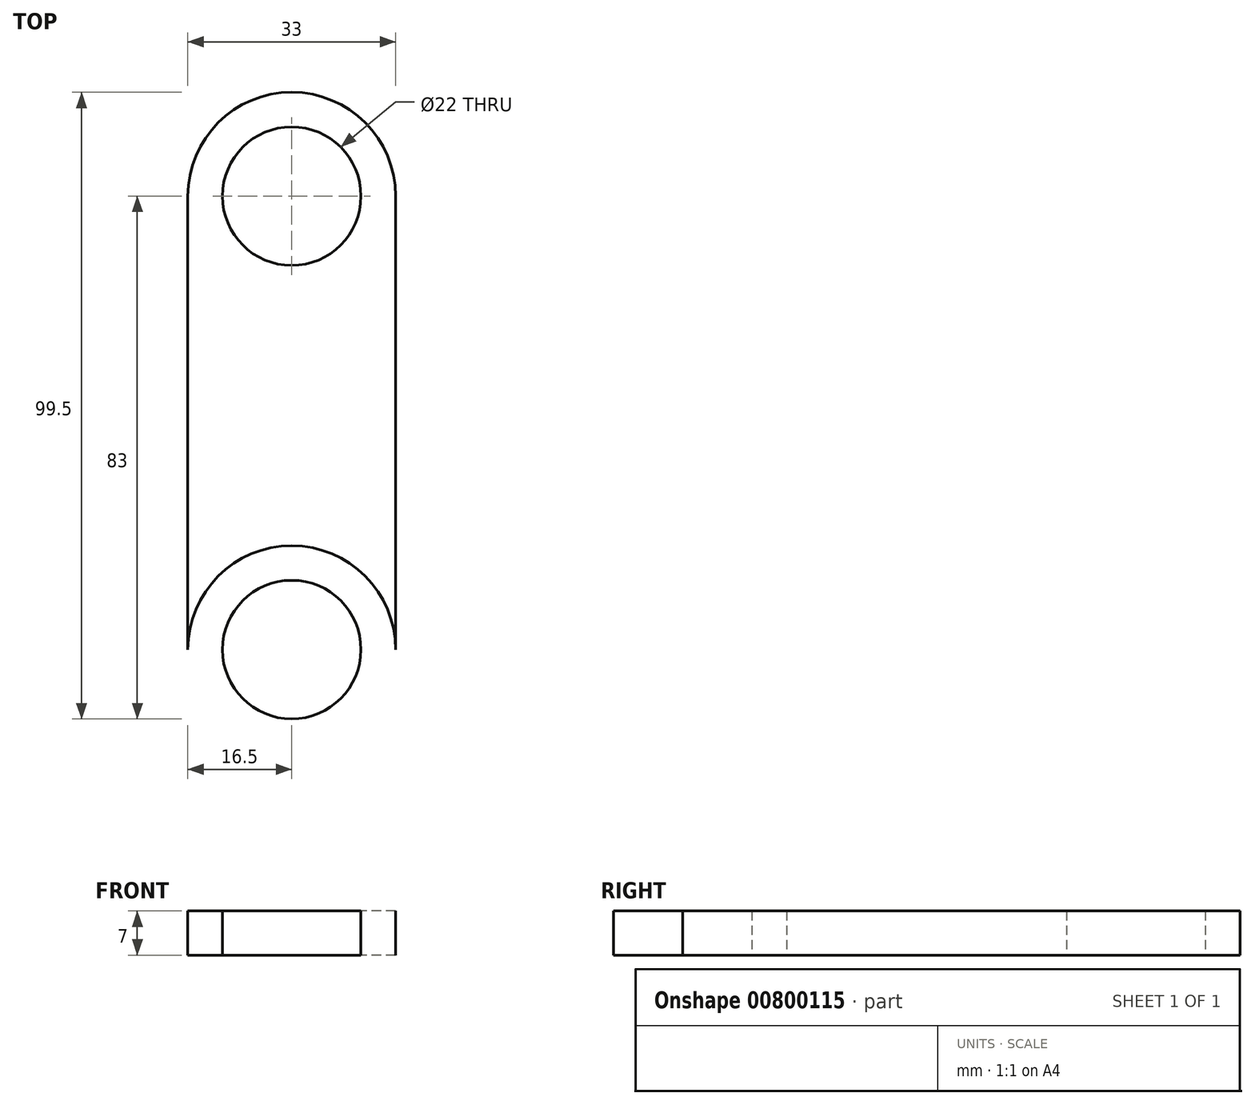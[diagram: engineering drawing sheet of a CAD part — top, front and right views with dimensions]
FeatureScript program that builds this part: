
annotation { "Feature Type Name" : "Feature", "Feature Type Description" : "" }
export const myFeature = defineFeature(function(context is Context, id is Id, definition is map)
    precondition{}
    {
        {
            var Q0;
            Q0=qCreatedBy(makeId("Top.planeOp"),FACE);
            var sketch = newSketch(context, id + "F0", { "sketchPlane" : qUnion([Q0])});
            skCircle(sketch, "E0", {"center": v(0, 0) * mm, "radius": 11 * mm});
            skCircle(sketch, "E1", {"center": v(0, 0) * mm, "radius": 16.5 * mm});
            skLineSegment(sketch, "E2", {"start": v(0, 0) * mm, "end": v(0, 36) * mm});
            skCircle(sketch, "E3", {"center": v(0, 36) * mm, "radius": 11 * mm});
            skCircle(sketch, "E4", {"center": v(0, 36) * mm, "radius": 16.5 * mm});
            skLineSegment(sketch, "E5", {"start": v(-16.5, 36) * mm, "end": v(-16.5, 0) * mm});
            skLineSegment(sketch, "E6", {"start": v(16.5, 36) * mm, "end": v(16.5, 0) * mm});
            skCircle(sketch, "E7.MirrorC", {"center": v(0, -36) * mm, "radius": 16.5 * mm});
            skCircle(sketch, "E8.MirrorC", {"center": v(0, -36) * mm, "radius": 11 * mm});
            skLineSegment(sketch, "E9.MirrorCS", {"start": v(-16.5, -36) * mm, "end": v(-16.5, 0) * mm});
            skLineSegment(sketch, "E10.MirrorCS", {"start": v(16.5, -36) * mm, "end": v(16.5, 0) * mm});
            skLineSegment(sketch, "E11.MirrorCS", {"start": v(0, 0) * mm, "end": v(0, -36) * mm});
            skSolve(sketch);
        }
        {
            var Q0;
            Q0=makeQuery(id+"F0.imprint","IMPRINT",FACE,{"disambiguationData":[TD([[makeQuery(id+"F0.imprint","IMPRINT",EDGE,{"derivedFrom":sQuery(id+"F0.wireOp",EDGE,"E3")}),-1.0]])]});
            var Q1;
            {var subQ0=sQuery(id+"F0.wireOp",EDGE,"E5");Q1=makeQuery(id+"F0.imprint","IMPRINT",FACE,{"disambiguationData":[TD([[makeQuery(id+"F0.imprint","IMPRINT",EDGE,{"derivedFrom":subQ0}),1.0]])]});}
            var Q2;
            Q2=makeQuery(id+"F0.imprint","IMPRINT",FACE,{"disambiguationData":[TD([[makeQuery(id+"F0.imprint","IMPRINT",EDGE,{"derivedFrom":sQuery(id+"F0.wireOp",EDGE,"E0")}),-1.0]])]});
            var Q3;
            {var subQ0=sQuery(id+"F0.wireOp",EDGE,"E6");Q3=makeQuery(id+"F0.imprint","IMPRINT",FACE,{"disambiguationData":[TD([[makeQuery(id+"F0.imprint","IMPRINT",EDGE,{"derivedFrom":subQ0}),-1.0]])]});}
            var Q4;
            Q4=makeQuery(id+"F0.imprint","IMPRINT",FACE,{"disambiguationData":[TD([[makeQuery(id+"F0.imprint","IMPRINT",EDGE,{"derivedFrom":sQuery(id+"F0.wireOp",EDGE,"w59R6iEj-CVUa-9ueu-Tdas-qJSk46i4Kriu")}),-1.0]])]});
            var Q5;
            {var subQ0=sQuery(id+"F0.wireOp",EDGE,"9POMkXtT-UIhR-gZSc-IBxU-MhUZsLWMQHKa");Q5=makeQuery(id+"F0.imprint","IMPRINT",FACE,{"disambiguationData":[TD([[makeQuery(id+"F0.imprint","IMPRINT",EDGE,{"derivedFrom":subQ0}),1.0]])]});}
            var Q6;
            {var subQ0=sQuery(id+"F0.wireOp",EDGE,"YCNqZ2w3-WSpD-Hsbr-H4GR-OdnoBN2QN9m9");Q6=makeQuery(id+"F0.imprint","IMPRINT",FACE,{"disambiguationData":[TD([[makeQuery(id+"F0.imprint","IMPRINT",EDGE,{"derivedFrom":subQ0}),-1.0]])]});}
            var Q7;
            {var subQ0=sQuery(id+"F0.wireOp",EDGE,"OA4v10v7-7EfV-4VX5-mn84-gwHHFcdyXIMs");Q7=makeQuery(id+"F0.imprint","IMPRINT",FACE,{"disambiguationData":[TD([[makeQuery(id+"F0.imprint","IMPRINT",EDGE,{"derivedFrom":subQ0}),1.0]])]});}
            var Q8;
            {var subQ0=sQuery(id+"F0.wireOp",EDGE,"jbeIYnq7-oU1V-4uXr-7pWT-a0tOQSGMHwd7");Q8=makeQuery(id+"F0.imprint","IMPRINT",FACE,{"disambiguationData":[TD([[makeQuery(id+"F0.imprint","IMPRINT",EDGE,{"derivedFrom":subQ0}),-1.0]])]});}
            var Q9;
            Q9=makeQuery(id+"F0.imprint","IMPRINT",FACE,{"disambiguationData":[TD([[makeQuery(id+"F0.imprint","IMPRINT",EDGE,{"derivedFrom":sQuery(id+"F0.wireOp",EDGE,"yAsJW6Uh-ad33-APdP-WKjL-GoX4Km3I4IXD")}),-1.0]])]});
            var Q10;
            {var subQ1=sQuery(id+"F0.wireOp",EDGE,"E0");var subQ6=sQuery(id+"F0.wireOp",EDGE,"4abtu9ri-UXn3-SYOI-gj1q-We8Vol63bBBD");var subQ8=makeQuery(id+"F0.imprint","INTERSECT",VERTEX,{"derivedFrom":[subQ1,subQ6]});Q10=makeQuery(id+"F0.imprint","IMPRINT",FACE,{"disambiguationData":[TD([[makeQuery(id+"F0.imprint","IMPRINT",EDGE,{"disambiguationData":[TD([[subQ8,1.0]])],"derivedFrom":subQ1}),-1.0]])]});}
            var Q11;
            {var subQ0=sQuery(id+"F0.wireOp",EDGE,"E2");var subQ1=sQuery(id+"F0.wireOp",EDGE,"E0");var subQ2=makeQuery(id+"F0.imprint","INTERSECT",VERTEX,{"derivedFrom":[subQ1,subQ0]});Q11=makeQuery(id+"F0.imprint","IMPRINT",FACE,{"disambiguationData":[TD([[makeQuery(id+"F0.imprint","IMPRINT",EDGE,{"disambiguationData":[TD([[subQ2,1.0]])],"derivedFrom":subQ1}),-1.0]])]});}
            var Q12;
            {var subQ0=sQuery(id+"F0.wireOp",EDGE,"4abtu9ri-UXn3-SYOI-gj1q-We8Vol63bBBD");var subQ1=sQuery(id+"F0.wireOp",EDGE,"E1");var subQ2=makeQuery(id+"F0.imprint","INTERSECT",VERTEX,{"derivedFrom":[subQ1,subQ0]});Q12=makeQuery(id+"F0.imprint","IMPRINT",FACE,{"disambiguationData":[TD([[makeQuery(id+"F0.imprint","IMPRINT",EDGE,{"disambiguationData":[TD([[subQ2,-1.0]])],"derivedFrom":subQ1}),-1.0]])]});}
            var Q13;
            Q13=makeQuery(id+"F0.imprint","IMPRINT",FACE,{"disambiguationData":[TD([[makeQuery(id+"F0.imprint","IMPRINT",EDGE,{"derivedFrom":sQuery(id+"F0.wireOp",EDGE,"gPTZF1Z9-XTqS-HgNZ-dHx2-uuJqNWMW2OWi")}),-1.0]])]});
            var Q14;
            Q14=makeQuery(id+"F0.imprint","IMPRINT",FACE,{"disambiguationData":[TD([[makeQuery(id+"F0.imprint","IMPRINT",EDGE,{"derivedFrom":sQuery(id+"F0.wireOp",EDGE,"pRESw98m-a7WB-Kv5g-NeYZ-crrq8cEqRvqA")}),-1.0]])]});
            var Q15;
            {var subQ0=sQuery(id+"F0.wireOp",EDGE,"UsmJrRAo-XE7W-iZRG-moOh-7sXpja8KDNIC");Q15=makeQuery(id+"F0.imprint","IMPRINT",FACE,{"disambiguationData":[TD([[makeQuery(id+"F0.imprint","IMPRINT",EDGE,{"derivedFrom":subQ0}),1.0]])]});}
            var Q16;
            {var subQ0=sQuery(id+"F0.wireOp",EDGE,"VRhz7LU3-4j0L-Ptb6-b6TJ-dEu7l9a6t27P");Q16=makeQuery(id+"F0.imprint","IMPRINT",FACE,{"disambiguationData":[TD([[makeQuery(id+"F0.imprint","IMPRINT",EDGE,{"derivedFrom":subQ0}),-1.0]])]});}
            var Q17;
            {var subQ5=sQuery(id+"F0.wireOp",EDGE,"E0");var subQ7=sQuery(id+"F0.wireOp",EDGE,"kRj30VAH-6UNE-fOCm-j82z-aHaWqIesx49l");var subQ9=makeQuery(id+"F0.imprint","INTERSECT",VERTEX,{"derivedFrom":[subQ5,subQ7]});Q17=makeQuery(id+"F0.imprint","IMPRINT",FACE,{"disambiguationData":[TD([[makeQuery(id+"F0.imprint","IMPRINT",EDGE,{"disambiguationData":[TD([[subQ9,-1.0]])],"derivedFrom":subQ5}),-1.0]])]});}
            var Q18;
            Q18=makeQuery(id+"F0.imprint","IMPRINT",FACE,{"disambiguationData":[TD([[makeQuery(id+"F0.imprint","IMPRINT",EDGE,{"derivedFrom":sQuery(id+"F0.wireOp",EDGE,"upXqz5X1-IKzU-vpSb-smbU-0F3NzNdugzUz")}),-1.0]])]});
            var Q19;
            {var subQ3=sQuery(id+"F0.wireOp",EDGE,"llwqtmrq-Y6AM-Iq4E-WuEU-azelPJxb1tUK");var subQ7=sQuery(id+"F0.wireOp",EDGE,"E1");var subQ9=makeQuery(id+"F0.imprint","INTERSECT",VERTEX,{"derivedFrom":[subQ7,subQ3]});Q19=makeQuery(id+"F0.imprint","IMPRINT",FACE,{"disambiguationData":[TD([[makeQuery(id+"F0.imprint","IMPRINT",EDGE,{"disambiguationData":[TD([[subQ9,1.0]])],"derivedFrom":subQ7}),-1.0]])]});}
            var Q20;
            {var subQ0=sQuery(id+"F0.wireOp",EDGE,"pKvLyjl6-diYY-jxjx-DDhw-XRv2EEQCgdWn");var subQ1=sQuery(id+"F0.wireOp",EDGE,"E1");var subQ2=makeQuery(id+"F0.imprint","INTERSECT",VERTEX,{"derivedFrom":[subQ1,subQ0]});Q20=makeQuery(id+"F0.imprint","IMPRINT",FACE,{"disambiguationData":[TD([[makeQuery(id+"F0.imprint","IMPRINT",EDGE,{"disambiguationData":[TD([[subQ2,-1.0]])],"derivedFrom":subQ1}),-1.0]])]});}
            var Q21;
            Q21=makeQuery(id+"F0.imprint","IMPRINT",FACE,{"disambiguationData":[TD([[makeQuery(id+"F0.imprint","IMPRINT",EDGE,{"derivedFrom":sQuery(id+"F0.wireOp",EDGE,"vxNKHGDU-jruf-Yhw1-oMMH-Wxl8c9OFgPlw")}),-1.0]])]});
            var Q22;
            {var subQ0=sQuery(id+"F0.wireOp",EDGE,"tUhpeLZv-qzEC-kt7y-z1LI-ajgduP5IIdtg");Q22=makeQuery(id+"F0.imprint","IMPRINT",FACE,{"disambiguationData":[TD([[makeQuery(id+"F0.imprint","IMPRINT",EDGE,{"derivedFrom":subQ0}),1.0]])]});}
            var Q23;
            {var subQ5=sQuery(id+"F0.wireOp",EDGE,"E5");Q23=makeQuery(id+"F0.imprint","IMPRINT",FACE,{"disambiguationData":[TD([[makeQuery(id+"F0.imprint","IMPRINT",EDGE,{"derivedFrom":subQ5}),1.0]])]});}
            var Q24;
            {var subQ2=sQuery(id+"F0.wireOp",EDGE,"E2");var subQ4=sQuery(id+"F0.wireOp",EDGE,"E0");var subQ8=makeQuery(id+"F0.imprint","INTERSECT",VERTEX,{"derivedFrom":[subQ2,subQ4]});Q24=makeQuery(id+"F0.imprint","IMPRINT",FACE,{"disambiguationData":[TD([[makeQuery(id+"F0.imprint","IMPRINT",EDGE,{"disambiguationData":[TD([[subQ8,-1.0]])],"derivedFrom":subQ2}),1.0]])]});}
            var Q25;
            {var subQ0=sQuery(id+"F0.wireOp",EDGE,"E0");var subQ1=sQuery(id+"F0.wireOp",EDGE,"E2");var subQ2=makeQuery(id+"F0.imprint","INTERSECT",VERTEX,{"derivedFrom":[subQ1,subQ0]});Q25=makeQuery(id+"F0.imprint","IMPRINT",FACE,{"disambiguationData":[TD([[makeQuery(id+"F0.imprint","IMPRINT",EDGE,{"disambiguationData":[TD([[subQ2,-1.0]])],"derivedFrom":subQ1}),-1.0]])]});}
            var Q26;
            {var subQ0=sQuery(id+"F0.wireOp",EDGE,"E9.MirrorCS");Q26=makeQuery(id+"F0.imprint","IMPRINT",FACE,{"disambiguationData":[TD([[makeQuery(id+"F0.imprint","IMPRINT",EDGE,{"derivedFrom":subQ0}),-1.0]])]});}
            var Q27;
            Q27=makeQuery(id+"F0.imprint","IMPRINT",FACE,{"disambiguationData":[TD([[makeQuery(id+"F0.imprint","IMPRINT",EDGE,{"derivedFrom":sQuery(id+"F0.wireOp",EDGE,"E8.MirrorC")}),1.0]])]});
            var Q28;
            {var subQ0=sQuery(id+"F0.wireOp",EDGE,"E10.MirrorCS");Q28=makeQuery(id+"F0.imprint","IMPRINT",FACE,{"disambiguationData":[TD([[makeQuery(id+"F0.imprint","IMPRINT",EDGE,{"derivedFrom":subQ0}),1.0]])]});}
            extrude(context, id + "F1", {"entities" : qUnion([Q0, Q1, Q2, Q3, Q4, Q5, Q6, Q7, Q8, Q9, Q10, Q11, Q12, Q13, Q14, Q15, Q16, Q17, Q18, Q19, Q20, Q21, Q22, Q23, Q24, Q25, Q26, Q27, Q28]), "depth" : 7 * mm, "offsetDistance" : 25 * mm});
        }
    });
